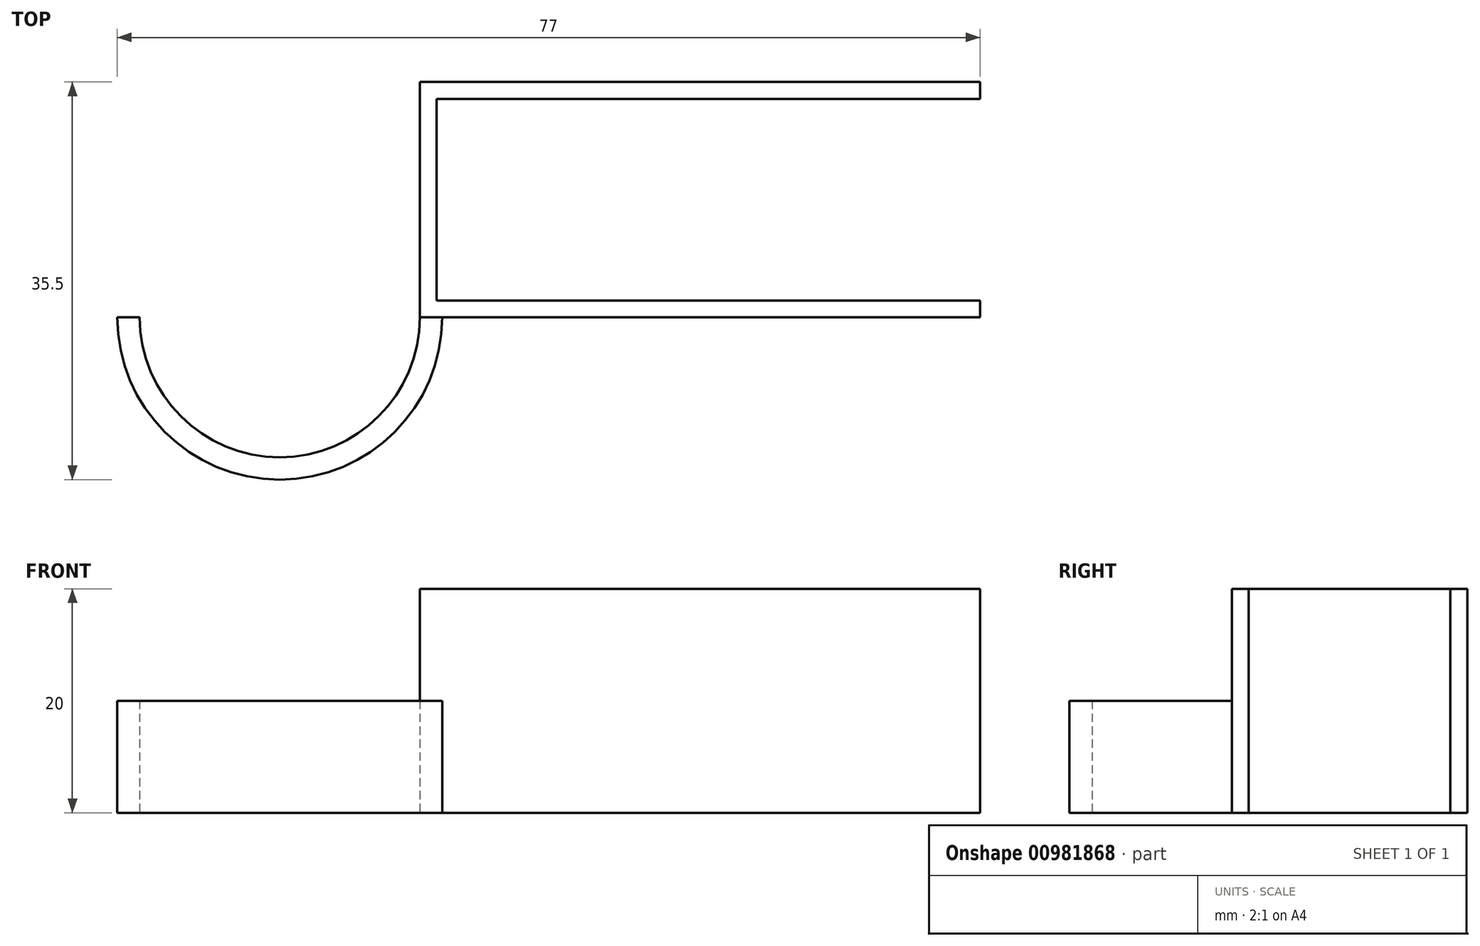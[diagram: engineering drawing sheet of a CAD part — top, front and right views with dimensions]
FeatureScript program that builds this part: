
annotation { "Feature Type Name" : "Feature", "Feature Type Description" : "" }
export const myFeature = defineFeature(function(context is Context, id is Id, definition is map)
    precondition{}
    {
        {
            var Q0;
            Q0=qCreatedBy(makeId("Top.planeOp"),FACE);
            var sketch = newSketch(context, id + "F0", { "sketchPlane" : qUnion([Q0])});
            skLineSegment(sketch, "E0.MirrorCS", {"start": v(-75, 0) * mm, "end": v(-77, 0) * mm});
            skLineSegment(sketch, "E1.MirrorCS", {"start": v(0, 21) * mm, "end": v(-50, 21) * mm});
            skLineSegment(sketch, "E2.MirrorCS", {"start": v(0, 19.5) * mm, "end": v(-48.5, 19.5) * mm});
            skLineSegment(sketch, "E3.MirrorCS", {"start": v(0, 0) * mm, "end": v(-50, 0) * mm});
            skLineSegment(sketch, "E4.MirrorCS", {"start": v(0, 1.5) * mm, "end": v(-48.5, 1.5) * mm});
            skArc(sketch, "E5.MirrorCS", {"start": v(-48, 0) * mm, "mid": v(-62.5, -14.5) * mm, "end": v(-77, 0) * mm});
            skLineSegment(sketch, "E6.MirrorCS", {"start": v(-48.5, 19.5) * mm, "end": v(-48.5, 1.5) * mm});
            skLineSegment(sketch, "E7.MirrorCS", {"start": v(-50, 0) * mm, "end": v(-50, 21) * mm});
            skArc(sketch, "E8.MirrorCS", {"start": v(-50, 0) * mm, "mid": v(-62.5, -12.5) * mm, "end": v(-75, 0) * mm});
            skLineSegment(sketch, "E9", {"start": v(0, 21) * mm, "end": v(0, 19.5) * mm});
            skLineSegment(sketch, "E10", {"start": v(0, 1.5) * mm, "end": v(0, 0) * mm});
            skSolve(sketch);
        }
        {
            var Q0;
            Q0=makeQuery(id+"F0.imprint","IMPRINT",FACE,{"disambiguationData":[TD([[makeQuery(id+"F0.imprint","IMPRINT",EDGE,{"derivedFrom":sQuery(id+"F0.wireOp",EDGE,"7u7ED2pA-vjBk-xvnc-XakZ-ugQEH75jc4Gw.top")}),-1.0]])]});
            var Q1;
            Q1=makeQuery(id+"F0.imprint","IMPRINT",FACE,{"disambiguationData":[TD([[makeQuery(id+"F0.imprint","IMPRINT",EDGE,{"derivedFrom":sQuery(id+"F0.wireOp",EDGE,"E1.MirrorCS")}),1.0]])]});
            extrude(context, id + "F1", {"entities" : qUnion([Q0, Q1]), "depth" : 20 * mm, "offsetDistance" : 25 * mm});
        }
        {
            var Q0;
            {var subQ0=sQuery(id+"F0.wireOp",EDGE,"ney9TRkq-mhuU-rV66-3d2e-6UzBLdOWi4nr");Q0=makeQuery(id+"F0.imprint","IMPRINT",FACE,{"disambiguationData":[TD([[makeQuery(id+"F0.imprint","IMPRINT",EDGE,{"derivedFrom":subQ0}),-1.0]])]});}
            var Q1;
            Q1=makeQuery(id+"F0.imprint","IMPRINT",FACE,{"disambiguationData":[TD([[makeQuery(id+"F0.imprint","IMPRINT",EDGE,{"derivedFrom":sQuery(id+"F0.wireOp",EDGE,"E0.MirrorCS")}),1.0]])]});
            extrude(context, id + "F2", {"entities" : qUnion([Q0, Q1]), "operationType" : NewBodyOperationType.ADD, "depth" : 10 * mm, "offsetDistance" : 25 * mm});
        }
    });
